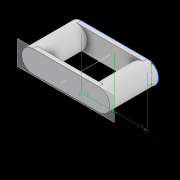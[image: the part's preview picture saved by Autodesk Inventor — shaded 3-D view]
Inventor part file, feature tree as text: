
AUTODESK INVENTOR PART (.ipt)
format: ipt  version: 2022.2 (Build 262287010, 287A)  size: 106,496 bytes
history: native  units: mm
features: extrude x3, projected_geometry x3, sketch x2, plane x1
ambient origin geometry x8: Origin, YZ Plane, XZ Plane, XY Plane, X Axis, Y Axis, Z Axis, Center Point
bodies: Solid1 (feature_tree)
feature tree (9):
  sketch  "Sketch1"  dims[d1=5.0mm d2=1.0mm d3=0.0mm]
  extrude  "Extrusion1"  Depth=1.0mm TaperAngle=0.0deg
  extrude  "Extrusion2"  Depth=7.5mm
  plane  "Work Plane1"
  extrude  "Extrusion3"  Depth=7.5mm
  sketch  "Sketch2"  dims[d4=10.0mm d5=0.0mm d9=7.5mm d10=7.5mm d11=11.0mm d12=1.0mm d13=0.0mm]
  projected_geometry  "Projected Loop1"
  projected_geometry  "Projected Loop2"
  projected_geometry  "Projected Loop3"
